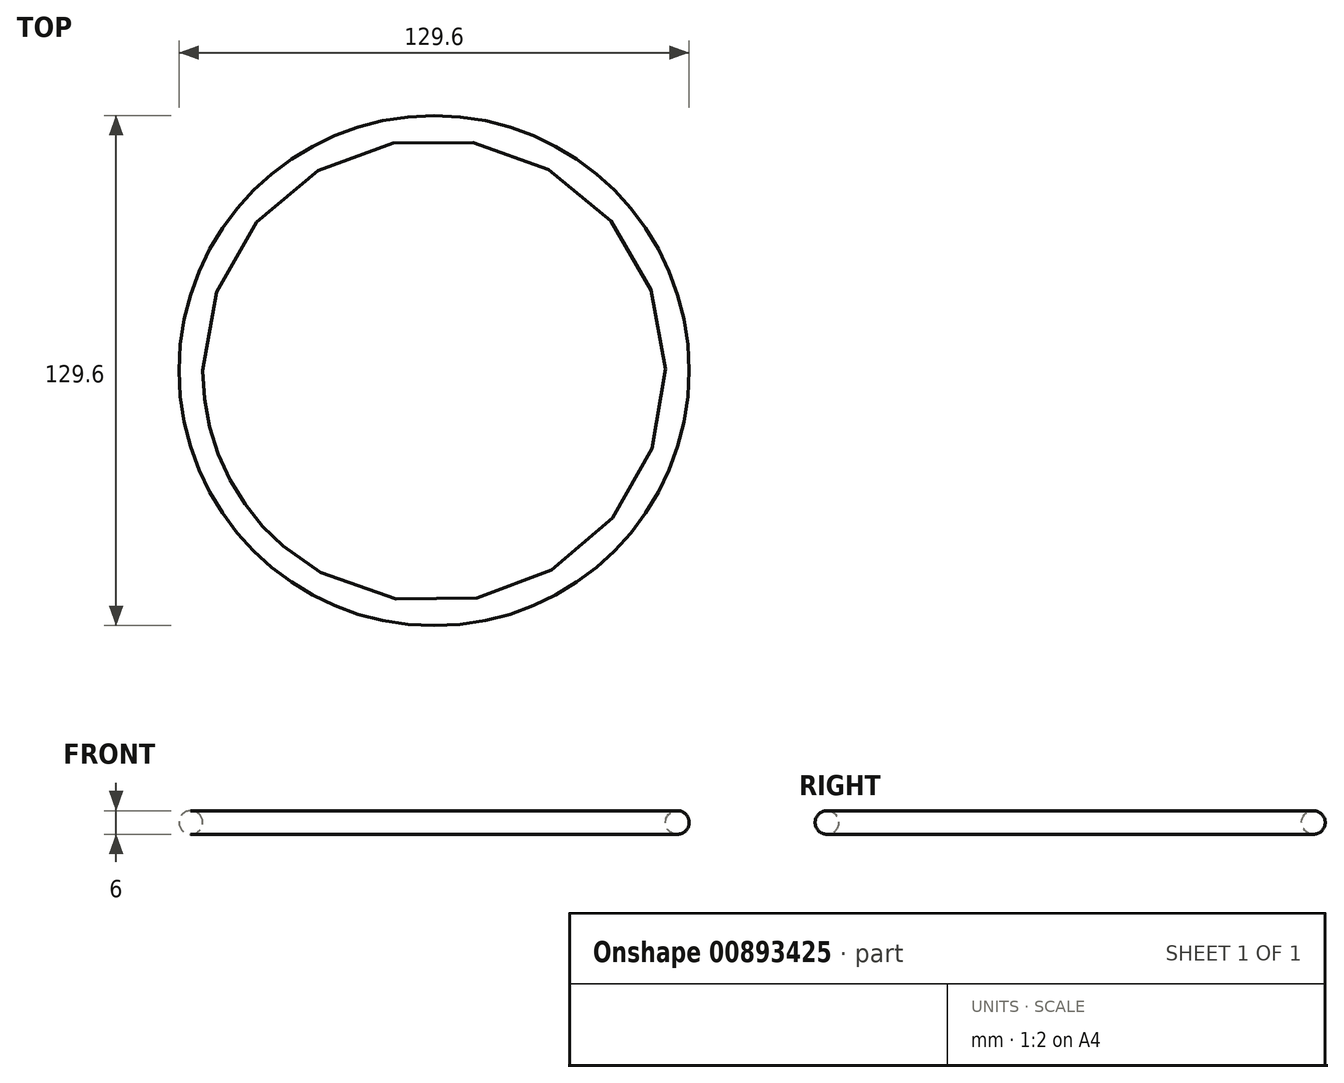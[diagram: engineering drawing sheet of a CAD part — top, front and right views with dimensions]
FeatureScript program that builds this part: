
annotation { "Feature Type Name" : "Feature", "Feature Type Description" : "" }
export const myFeature = defineFeature(function(context is Context, id is Id, definition is map)
    precondition{}
    {
        {
            var Q0;
            Q0=qCreatedBy(makeId("Front.planeOp"),FACE);
            var sketch = newSketch(context, id + "F0", { "sketchPlane" : qUnion([Q0])});
            skCircle(sketch, "E0", {"center": v(-61.8, 0) * mm, "radius": 3 * mm});
            skLineSegment(sketch, "E1", {"start": v(0, 0) * mm, "end": v(0, 21.31) * mm});
            skSolve(sketch);
        }
        {
            var Q0;
            Q0=makeQuery(id+"F0.imprint","IMPRINT",FACE,{"disambiguationData":[TD([[makeQuery(id+"F0.imprint","IMPRINT",EDGE,{"derivedFrom":sQuery(id+"F0.wireOp",EDGE,"E0")}),1.0]])]});
            var Q1;
            Q1=sQuery(id+"F0.wireOp",EDGE,"E1");
            revolve(context, id + "F1", {"surfaceOperationType" : NewSurfaceOperationType.NEW, "entities" : qUnion([Q0]), "axis" : qUnion([Q1]), "revolveType" : RevolveType.FULL});
        }
    });
